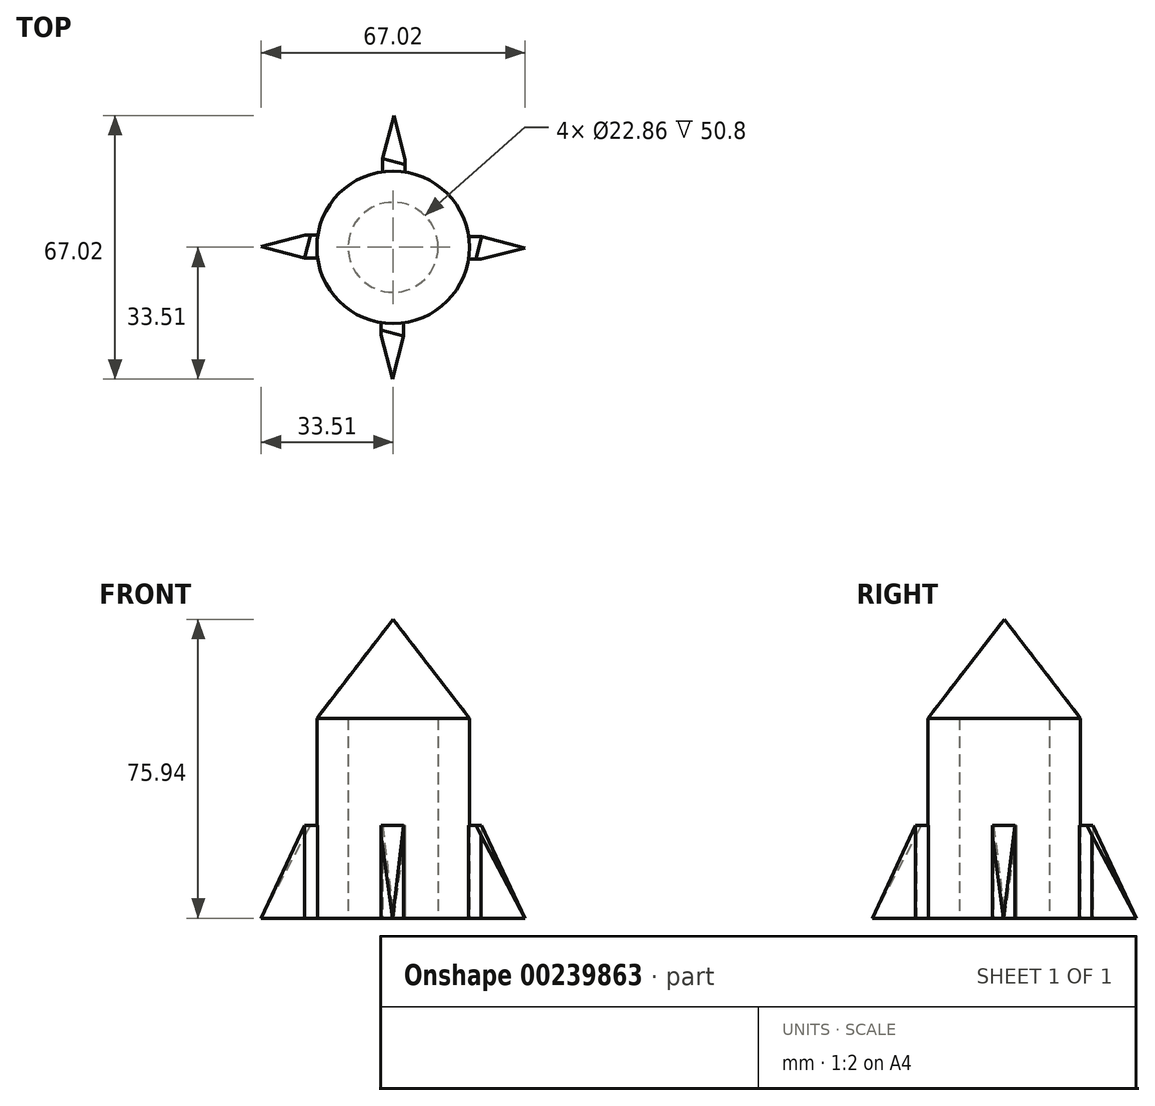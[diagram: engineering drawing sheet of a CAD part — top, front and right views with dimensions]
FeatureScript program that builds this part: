
annotation { "Feature Type Name" : "Feature", "Feature Type Description" : "" }
export const myFeature = defineFeature(function(context is Context, id is Id, definition is map)
    precondition{}
    {
        {
            var Q0;
            Q0=qCreatedBy(makeId("Front.planeOp"),FACE);
            var sketch = newSketch(context, id + "F0", { "sketchPlane" : qUnion([Q0])});
            skLineSegment(sketch, "E0", {"start": v(-11.43, 13.86) * mm, "end": v(-11.43, 39.26) * mm});
            skLineSegment(sketch, "E1", {"start": v(-11.43, 39.26) * mm, "end": v(0, 39.26) * mm});
            skLineSegment(sketch, "E2", {"start": v(0, 39.26) * mm, "end": v(0, 64.4) * mm});
            skPoint(sketch, "E3.endSnap0", {"position": v(0, 51.83) * mm});
            skLineSegment(sketch, "E4", {"start": v(0, 64.4) * mm, "end": v(0, -11.54) * mm, "construction": true});
            skLineSegment(sketch, "E5", {"start": v(0, -11.54) * mm, "end": v(-11.43, -11.54) * mm, "construction": true});
            skLineSegment(sketch, "E6", {"start": v(-11.43, -11.54) * mm, "end": v(-19.38, -11.54) * mm, "construction": true});
            skLineSegment(sketch, "E7", {"start": v(-19.38, -11.54) * mm, "end": v(-19.38, 39.26) * mm});
            skLineSegment(sketch, "E8", {"start": v(-19.38, 39.26) * mm, "end": v(0, 64.4) * mm});
            skLineSegment(sketch, "E9", {"start": v(-11.43, 13.86) * mm, "end": v(-11.43, -11.54) * mm});
            skLineSegment(sketch, "E10", {"start": v(-11.43, -11.54) * mm, "end": v(-19.38, -11.54) * mm});
            skSolve(sketch);
        }
        {
            var Q0;
            Q0=makeQuery(id+"F0.imprint","IMPRINT",FACE,{"disambiguationData":[TD([[makeQuery(id+"F0.imprint","IMPRINT",EDGE,{"derivedFrom":sQuery(id+"F0.wireOp",EDGE,"E0")}),1.0]])]});
            var Q1;
            Q1=sQuery(id+"F0.wireOp",EDGE,"E2");
            revolve(context, id + "F1", {"entities" : qUnion([Q0]), "axis" : qUnion([Q1]), "revolveType" : RevolveType.FULL});
        }
        {
            var Q0;
            Q0=makeQuery(id+"F1.opRevolve","SWEPT_FACE",FACE,{"disambiguationData":[OSD([sQuery(id+"F0.wireOp",EDGE,"E10")])]});
            var sketch = newSketch(context, id + "F2", { "sketchPlane" : qUnion([Q0])});
            skLineSegment(sketch, "E11", {"start": v(-2.7, -11.53) * mm, "end": v(-2.7, -33.51) * mm});
            skLineSegment(sketch, "E12", {"start": v(-2.7, -33.51) * mm, "end": v(3.05, -33.51) * mm});
            skLineSegment(sketch, "E13", {"start": v(3.05, -33.51) * mm, "end": v(3.05, -11.13) * mm});
            skLineSegment(sketch, "E14", {"start": v(3.05, -11.13) * mm, "end": v(-2.7, -11.53) * mm});
            skLineSegment(sketch, "E15", {"start": v(-2.7, -22.52) * mm, "end": v(0.18, -33.51) * mm});
            skLineSegment(sketch, "E16", {"start": v(0.18, -33.51) * mm, "end": v(3.05, -22.32) * mm});
            skSolve(sketch);
        }
        {
            var Q0;
            {var subQ4=sQuery(id+"F2.wireOp",EDGE,"E15");Q0=makeQuery(id+"F2.imprint","IMPRINT",FACE,{"disambiguationData":[TD([[makeQuery(id+"F2.imprint","IMPRINT",EDGE,{"derivedFrom":subQ4}),1.0]])]});}
            extrude(context, id + "F3", {"entities" : qUnion([Q0]), "operationType" : NewBodyOperationType.ADD, "oppositeDirection" : true, "depth" : 23.62 * mm});
        }
        {
            var Q0;
            Q0=makeQuery(id+"F3.opExtrude","SWEPT_FACE",FACE,{"disambiguationData":[OSD([sQuery(id+"F2.wireOp",EDGE,"E15")])]});
            var sketch = newSketch(context, id + "F4", { "sketchPlane" : qUnion([Q0])});
            skLineSegment(sketch, "E17", {"start": v(-21.11, 12.08) * mm, "end": v(-32.47, -11.54) * mm});
            skLineSegment(sketch, "E18", {"start": v(-32.47, -11.54) * mm, "end": v(-32.47, 12.08) * mm});
            skLineSegment(sketch, "E19", {"start": v(-32.47, 12.08) * mm, "end": v(-21.11, 12.08) * mm});
            skSolve(sketch);
        }
        {
            var Q0;
            Q0=makeQuery(id+"F4.imprint","IMPRINT",FACE,{"disambiguationData":[TD([[makeQuery(id+"F4.imprint","IMPRINT",EDGE,{"derivedFrom":sQuery(id+"F4.wireOp",EDGE,"E17")}),-1.0]])]});
            extrude(context, id + "F5", {"entities" : qUnion([Q0]), "operationType" : NewBodyOperationType.REMOVE, "oppositeDirection" : true, "depth" : 267.2 * mm});
        }
        {
            var Q0;
            Q0=qCreatedBy(makeId("Right.planeOp"),FACE);
            var sketch = newSketch(context, id + "F6", { "sketchPlane" : qUnion([Q0])});
            skLineSegment(sketch, "E20", {"start": v(0, 71.2) * mm, "end": v(0, -21.97) * mm, "construction": true});
            skSolve(sketch);
        }
        {
            var Q0;
            Q0=makeQuery(id+"F1.opRevolve","SWEPT_BODY",BODY,{"disambiguationData":[OSD([sQuery(id+"F0.wireOp",EDGE,"E0"),sQuery(id+"F0.wireOp",EDGE,"E1"),sQuery(id+"F0.wireOp",EDGE,"E2"),sQuery(id+"F0.wireOp",EDGE,"E7"),sQuery(id+"F0.wireOp",EDGE,"E8"),sQuery(id+"F0.wireOp",EDGE,"E9"),sQuery(id+"F0.wireOp",EDGE,"E10")])]});
            var Q1;
            Q1=sQuery(id+"F6.wireOp",EDGE,"E20");
            circularPattern(context, id + "F7", {"entities" : qUnion([Q0]), "axis" : qUnion([Q1]), "angle" : 360 * degree, "instanceCount" : 4, "equalSpace" : true});
        }
    });
